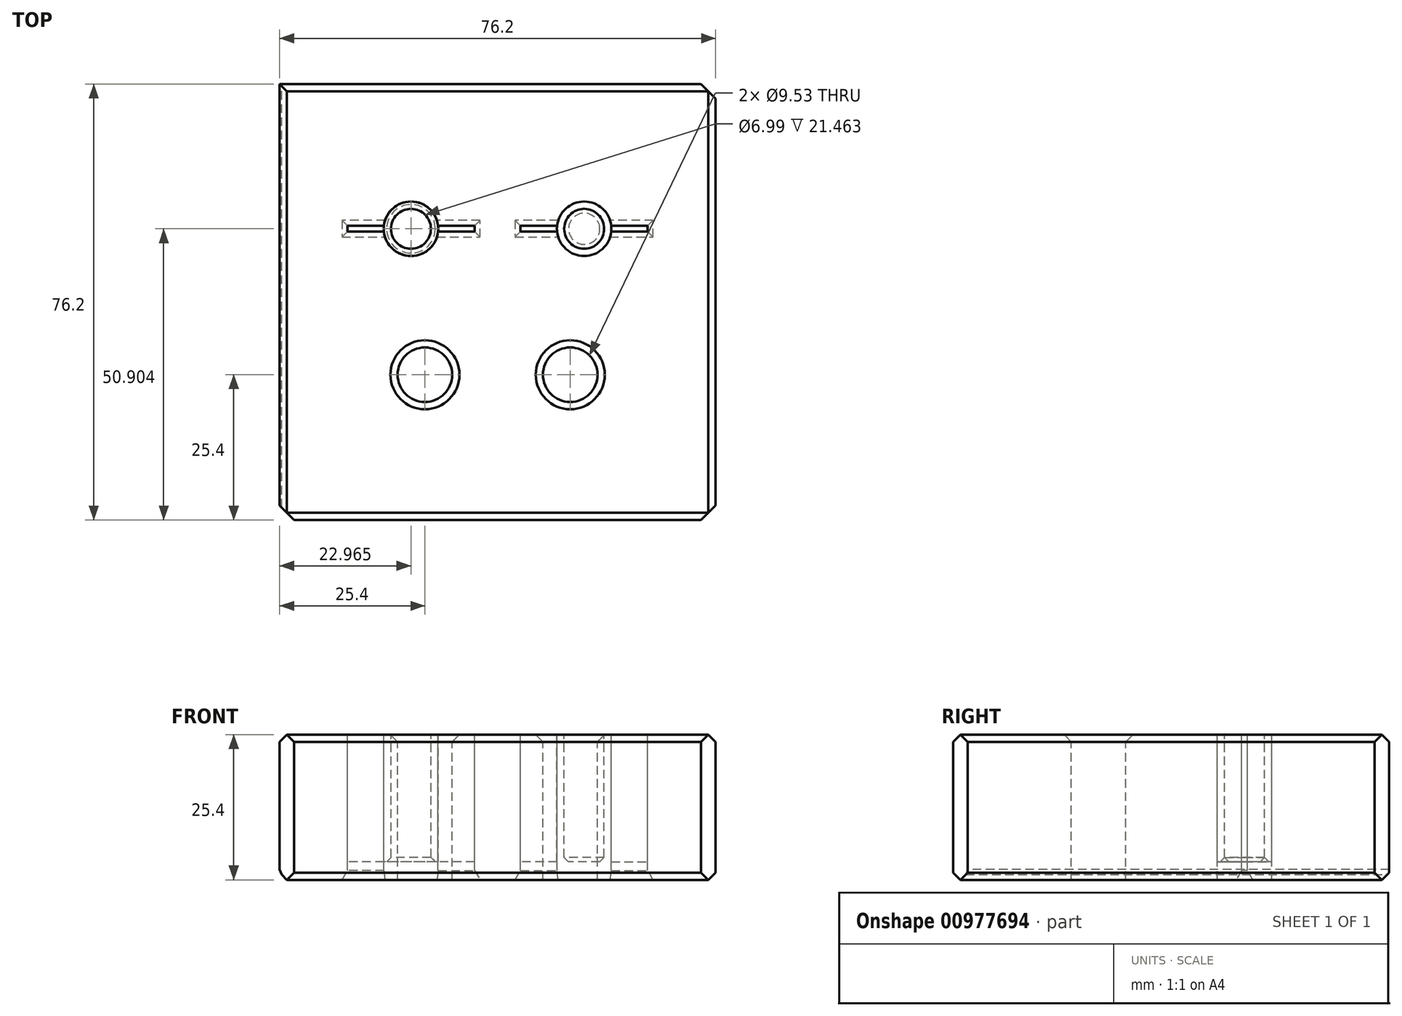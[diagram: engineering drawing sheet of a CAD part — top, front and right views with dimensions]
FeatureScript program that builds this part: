
annotation { "Feature Type Name" : "Feature", "Feature Type Description" : "" }
export const myFeature = defineFeature(function(context is Context, id is Id, definition is map)
    precondition{}
    {
        {
            var Q0;
            Q0=qCreatedBy(makeId("Top.planeOp"),FACE);
            var sketch = newSketch(context, id + "F0", { "sketchPlane" : qUnion([Q0])});
            skLineSegment(sketch, "E0.bottom", {"start": v(-38.1, 38.1) * mm, "end": v(38.1, 38.1) * mm});
            skLineSegment(sketch, "E0.top", {"start": v(-38.1, -38.1) * mm, "end": v(38.1, -38.1) * mm});
            skLineSegment(sketch, "E0.left", {"start": v(-38.1, 38.1) * mm, "end": v(-38.1, -38.1) * mm});
            skLineSegment(sketch, "E0.right", {"start": v(38.1, 38.1) * mm, "end": v(38.1, -38.1) * mm});
            skPoint(sketch, "E0.middle", {"position": v(0, 0) * mm});
            skPoint(sketch, "E1", {"position": v(-25.4, 38.1) * mm});
            skPoint(sketch, "E2.MirrorP", {"position": v(-25.4, -38.1) * mm});
            skPoint(sketch, "E3.MirrorP", {"position": v(25.4, 38.1) * mm});
            skPoint(sketch, "E4.MirrorP", {"position": v(25.4, -38.1) * mm});
            skPoint(sketch, "E5", {"position": v(-12.7, 38.1) * mm});
            skPoint(sketch, "E6", {"position": v(0, 38.1) * mm});
            skPoint(sketch, "E7", {"position": v(12.7, 38.1) * mm});
            skPoint(sketch, "E8", {"position": v(-12.7, -38.1) * mm});
            skPoint(sketch, "E9", {"position": v(-38.1, 25.4) * mm});
            skPoint(sketch, "E10", {"position": v(-38.1, 12.7) * mm});
            skPoint(sketch, "E11", {"position": v(-38.1, 0) * mm});
            skPoint(sketch, "E12.MirrorP", {"position": v(-38.1, -12.7) * mm});
            skPoint(sketch, "E13.MirrorP", {"position": v(-38.1, -25.4) * mm});
            skPoint(sketch, "E14.MirrorP", {"position": v(38.1, -25.4) * mm});
            skPoint(sketch, "E15.MirrorP", {"position": v(38.1, -12.7) * mm});
            skPoint(sketch, "E16.MirrorP", {"position": v(38.1, 0) * mm});
            skPoint(sketch, "E17.MirrorP", {"position": v(38.1, 12.7) * mm});
            skPoint(sketch, "E18.MirrorP", {"position": v(38.1, 25.4) * mm});
            skPoint(sketch, "E19", {"position": v(12.7, -38.1) * mm});
            skPoint(sketch, "E20", {"position": v(0, -38.1) * mm});
            skPoint(sketch, "E21", {"position": v(0, -25.4) * mm});
            skPoint(sketch, "E22", {"position": v(12.7, -25.4) * mm});
            skPoint(sketch, "E23", {"position": v(12.7, 25.4) * mm});
            skPoint(sketch, "E24", {"position": v(12.7, 0) * mm});
            skPoint(sketch, "E25", {"position": v(-13.1, 0) * mm});
            skLineSegment(sketch, "E26", {"start": v(0, 38.1) * mm, "end": v(0, -38.1) * mm});
            skPoint(sketch, "E27", {"position": v(-15.13, 12.8) * mm});
            skPoint(sketch, "E28", {"position": v(0, 12.7) * mm});
            skPoint(sketch, "E29", {"position": v(12.7, 12.7) * mm});
            skPoint(sketch, "E30", {"position": v(0, -12.7) * mm});
            skPoint(sketch, "E31", {"position": v(-12.7, -12.7) * mm});
            skPoint(sketch, "E32", {"position": v(12.7, -12.7) * mm});
            skPoint(sketch, "E33", {"position": v(53.16, 13.21) * mm});
            skCircle(sketch, "E34", {"center": v(-15.13, 12.8) * mm, "radius": 4.76 * mm});
            skCircle(sketch, "E35.MirrorC", {"center": v(15.13, 12.8) * mm, "radius": 4.76 * mm});
            skCircle(sketch, "E36.MirrorC", {"center": v(12.7, -12.7) * mm, "radius": 4.76 * mm});
            skCircle(sketch, "E37.MirrorC", {"center": v(-12.7, -12.7) * mm, "radius": 4.76 * mm});
            skLineSegment(sketch, "E38.left", {"start": v(-26.25, 13.31) * mm, "end": v(-26.25, 12.3) * mm});
            skLineSegment(sketch, "E38.right", {"start": v(-4.02, 13.31) * mm, "end": v(-4.02, 12.3) * mm});
            skArc(sketch, "E39", {"start": v(-10.4, 12.3) * mm, "mid": v(-10.37, 12.8) * mm, "end": v(-10.4, 13.31) * mm});
            skArc(sketch, "E40", {"start": v(-19.87, 13.31) * mm, "mid": v(-19.9, 12.8) * mm, "end": v(-19.87, 12.3) * mm});
            skLineSegment(sketch, "E41", {"start": v(-19.87, 13.31) * mm, "end": v(-26.25, 13.31) * mm});
            skLineSegment(sketch, "E42", {"start": v(-26.25, 12.3) * mm, "end": v(-19.87, 12.3) * mm});
            skLineSegment(sketch, "E43", {"start": v(-10.4, 13.31) * mm, "end": v(-4.02, 13.31) * mm});
            skLineSegment(sketch, "E44", {"start": v(-4.02, 12.3) * mm, "end": v(-10.4, 12.3) * mm});
            skCircle(sketch, "E45", {"center": v(-15.13, 12.8) * mm, "radius": 3.5 * mm});
            skCircle(sketch, "E46.MirrorC", {"center": v(15.13, 12.8) * mm, "radius": 3.5 * mm});
            skLineSegment(sketch, "E47.MirrorCS", {"start": v(10.4, 13.31) * mm, "end": v(4.02, 13.31) * mm});
            skLineSegment(sketch, "E48.MirrorCS", {"start": v(4.02, 12.3) * mm, "end": v(10.4, 12.3) * mm});
            skLineSegment(sketch, "E49.MirrorCS", {"start": v(4.02, 13.31) * mm, "end": v(4.02, 12.3) * mm});
            skLineSegment(sketch, "E50.MirrorCS", {"start": v(19.87, 13.31) * mm, "end": v(26.25, 13.31) * mm});
            skLineSegment(sketch, "E51.MirrorCS", {"start": v(26.25, 13.31) * mm, "end": v(26.25, 12.3) * mm});
            skLineSegment(sketch, "E52.MirrorCS", {"start": v(26.25, 12.3) * mm, "end": v(19.87, 12.3) * mm});
            skSolve(sketch);
        }
        {
            var Q0;
            {var subQ5=sQuery(id+"F0.wireOp",EDGE,"E0.left");Q0=makeQuery(id+"F0.imprint","IMPRINT",FACE,{"disambiguationData":[TD([[makeQuery(id+"F0.imprint","IMPRINT",EDGE,{"derivedFrom":subQ5}),1.0]])]});}
            var Q1;
            {var subQ1=sQuery(id+"F0.wireOp",EDGE,"E0.right");Q1=makeQuery(id+"F0.imprint","IMPRINT",FACE,{"disambiguationData":[TD([[makeQuery(id+"F0.imprint","IMPRINT",EDGE,{"derivedFrom":subQ1}),-1.0]])]});}
            extrude(context, id + "F1", {"entities" : qUnion([Q0, Q1]), "oppositeDirection" : true, "depth" : 25.4 * mm, "offsetDistance" : 25.4 * mm});
        }
        {
            var Q0;
            Q0=makeQuery(id+"F1.opExtrude","SWEPT_EDGE",EDGE,{"disambiguationData":[OSD([sQuery(id+"F0.wireOp",EDGE,"E0.top"),sQuery(id+"F0.wireOp",EDGE,"E0.right")])]});
            var Q1;
            Q1=makeQuery(id+"F1.opExtrude","SWEPT_EDGE",EDGE,{"disambiguationData":[OSD([sQuery(id+"F0.wireOp",EDGE,"E0.bottom"),sQuery(id+"F0.wireOp",EDGE,"E0.right")])]});
            var Q2;
            Q2=makeQuery(id+"F1.opExtrude","SWEPT_EDGE",EDGE,{"disambiguationData":[OSD([sQuery(id+"F0.wireOp",EDGE,"E0.top"),sQuery(id+"F0.wireOp",EDGE,"E0.left")])]});
            chamfer(context, id + "F2", {"entities" : qUnion([Q0, Q1, Q2]), "width" : 2.54 * mm, "tangentPropagation" : true});
        }
        {
            var Q0;
            Q0=makeQuery(id+"F1.opExtrude","CAP_EDGE",EDGE,{"disambiguationData":[OSD([sQuery(id+"F0.wireOp",EDGE,"E0.top")])],"isStart":true});
            var Q1;
            Q1=makeQuery(id+"F1.opExtrude","CAP_EDGE",EDGE,{"disambiguationData":[OSD([sQuery(id+"F0.wireOp",EDGE,"E0.bottom")])],"isStart":true});
            var Q2;
            Q2=makeQuery(id+"F1.opExtrude","CAP_EDGE",EDGE,{"disambiguationData":[OSD([sQuery(id+"F0.wireOp",EDGE,"E0.right")])],"isStart":true});
            var Q3;
            Q3=makeQuery(id+"F1.opExtrude","CAP_EDGE",EDGE,{"disambiguationData":[OSD([sQuery(id+"F0.wireOp",EDGE,"E0.right")])],"isStart":false});
            var Q4;
            Q4=makeQuery(id+"F1.opExtrude","CAP_EDGE",EDGE,{"disambiguationData":[OSD([sQuery(id+"F0.wireOp",EDGE,"E0.top")])],"isStart":false});
            var Q5;
            Q5=makeQuery(id+"F1.opExtrude","CAP_EDGE",EDGE,{"disambiguationData":[OSD([sQuery(id+"F0.wireOp",EDGE,"E0.bottom")])],"isStart":false});
            var Q6;
            Q6=makeQuery(id+"F1.opExtrude","CAP_EDGE",EDGE,{"disambiguationData":[OSD([sQuery(id+"F0.wireOp",EDGE,"E0.left")])],"isStart":false});
            chamfer(context, id + "F3", {"entities" : qUnion([Q0, Q1, Q2, Q3, Q4, Q5, Q6]), "width" : 1.27 * mm, "tangentPropagation" : true});
        }
        {
            var Q0;
            Q0=makeQuery(id+"F1.opExtrude","CAP_EDGE",EDGE,{"disambiguationData":[OSD([sQuery(id+"F0.wireOp",EDGE,"E0.left")])],"isStart":true});
            var Q1;
            {var subQ0=sQuery(id+"F0.wireOp",EDGE,"E0.left");Q1=makeQuery(id+"F3.opChamfer","BLEND_EDGE",EDGE,{"blendedFrom":[makeQuery(id+"F1.opExtrude","CAP_EDGE",EDGE,{"disambiguationData":[OSD([subQ0])],"isStart":false}),makeQuery(id+"F1.opExtrude","SWEPT_FACE",FACE,{"disambiguationData":[OSD([subQ0])]})],"blendedInto":[makeQuery(id+"F1.opExtrude","SWEPT_FACE",FACE,{"disambiguationData":[OSD([subQ0])]})]});}
            var Q2;
            Q2=makeQuery(id+"F1.opExtrude","CAP_EDGE",EDGE,{"disambiguationData":[OSD([sQuery(id+"F0.wireOp",EDGE,"E37.MirrorC")])],"isStart":true});
            var Q3;
            Q3=makeQuery(id+"F1.opExtrude","CAP_EDGE",EDGE,{"disambiguationData":[OSD([sQuery(id+"F0.wireOp",EDGE,"E36.MirrorC")])],"isStart":true});
            chamfer(context, id + "F4", {"entities" : qUnion([Q0, Q1, Q2, Q3]), "width" : 1.27 * mm, "tangentPropagation" : true});
        }
        {
            var Q0;
            Q0=makeQuery(id+"F0.imprint","IMPRINT",FACE,{"disambiguationData":[TD([[makeQuery(id+"F0.imprint","IMPRINT",EDGE,{"derivedFrom":sQuery(id+"F0.wireOp",EDGE,"E46.MirrorC")}),1.0]])]});
            var Q1;
            Q1=makeQuery(id+"F0.imprint","IMPRINT",FACE,{"disambiguationData":[TD([[makeQuery(id+"F0.imprint","IMPRINT",EDGE,{"derivedFrom":sQuery(id+"F0.wireOp",EDGE,"E45")}),-1.0]])]});
            var Q2;
            Q2=sQuery(id+"F0.wireOp",EDGE,"E46.MirrorC");
            var Q3;
            Q3=sQuery(id+"F0.wireOp",EDGE,"E35.MirrorC");
            extrude(context, id + "F5", {"entities" : qUnion([Q0, Q1]), "surfaceEntities" : qUnion([Q2, Q3]), "oppositeDirection" : true, "depth" : 22.22 * mm, "offsetDistance" : 25.4 * mm});
        }
        {
            var Q0;
            Q0=makeQuery(id+"F0.imprint","IMPRINT",FACE,{"disambiguationData":[TD([[makeQuery(id+"F0.imprint","IMPRINT",EDGE,{"derivedFrom":sQuery(id+"F0.wireOp",EDGE,"E38.right")}),-1.0]])]});
            var Q1;
            Q1=makeQuery(id+"F0.imprint","IMPRINT",FACE,{"disambiguationData":[TD([[makeQuery(id+"F0.imprint","IMPRINT",EDGE,{"derivedFrom":sQuery(id+"F0.wireOp",EDGE,"E38.left")}),1.0]])]});
            extrude(context, id + "F6", {"entities" : qUnion([Q0, Q1]), "oppositeDirection" : true, "depth" : 22.22 * mm, "offsetDistance" : 25.4 * mm});
        }
        {
            var Q0;
            {var subQ0=sQuery(id+"F0.wireOp",EDGE,"E47.MirrorCS");Q0=makeQuery(id+"F0.imprint","IMPRINT",FACE,{"disambiguationData":[TD([[makeQuery(id+"F0.imprint","IMPRINT",EDGE,{"derivedFrom":subQ0}),1.0]])]});}
            var Q1;
            {var subQ0=sQuery(id+"F0.wireOp",EDGE,"E50.MirrorCS");Q1=makeQuery(id+"F0.imprint","IMPRINT",FACE,{"disambiguationData":[TD([[makeQuery(id+"F0.imprint","IMPRINT",EDGE,{"derivedFrom":subQ0}),-1.0]])]});}
            extrude(context, id + "F7", {"entities" : qUnion([Q0, Q1]), "oppositeDirection" : true, "depth" : 22.22 * mm, "offsetDistance" : 25.4 * mm});
        }
        {
            var Q0;
            Q0=makeQuery(id+"F5.opExtrude","CAP_EDGE",EDGE,{"disambiguationData":[OSD([sQuery(id+"F0.wireOp",EDGE,"E46.MirrorC")])],"isStart":false});
            var Q1;
            Q1=makeQuery(id+"F5.opExtrude","CAP_EDGE",EDGE,{"disambiguationData":[OSD([sQuery(id+"F0.wireOp",EDGE,"E45")])],"isStart":false});
            chamfer(context, id + "F8", {"entities" : qUnion([Q0, Q1]), "width" : 0.76 * mm, "tangentPropagation" : true});
        }
        {
            var Q0;
            Q0=makeQuery(id+"F1.opExtrude","CAP_EDGE",EDGE,{"disambiguationData":[OSD([sQuery(id+"F0.wireOp",EDGE,"E42")])],"isStart":false});
            var Q1;
            Q1=makeQuery(id+"F1.opExtrude","CAP_EDGE",EDGE,{"disambiguationData":[OSD([sQuery(id+"F0.wireOp",EDGE,"E38.left")])],"isStart":false});
            var Q2;
            Q2=makeQuery(id+"F1.opExtrude","CAP_EDGE",EDGE,{"disambiguationData":[OSD([sQuery(id+"F0.wireOp",EDGE,"E41")])],"isStart":false});
            var Q3;
            Q3=makeQuery(id+"F1.opExtrude","CAP_EDGE",EDGE,{"disambiguationData":[OSD([sQuery(id+"F0.wireOp",EDGE,"E44")])],"isStart":false});
            var Q4;
            Q4=makeQuery(id+"F1.opExtrude","CAP_EDGE",EDGE,{"disambiguationData":[OSD([sQuery(id+"F0.wireOp",EDGE,"E38.right")])],"isStart":false});
            var Q5;
            Q5=makeQuery(id+"F1.opExtrude","CAP_EDGE",EDGE,{"disambiguationData":[OSD([sQuery(id+"F0.wireOp",EDGE,"E43")])],"isStart":false});
            var Q6;
            Q6=makeQuery(id+"F1.opExtrude","CAP_EDGE",EDGE,{"disambiguationData":[OSD([sQuery(id+"F0.wireOp",EDGE,"E48.MirrorCS")])],"isStart":false});
            var Q7;
            Q7=makeQuery(id+"F1.opExtrude","CAP_EDGE",EDGE,{"disambiguationData":[OSD([sQuery(id+"F0.wireOp",EDGE,"E49.MirrorCS")])],"isStart":false});
            var Q8;
            Q8=makeQuery(id+"F1.opExtrude","CAP_EDGE",EDGE,{"disambiguationData":[OSD([sQuery(id+"F0.wireOp",EDGE,"E47.MirrorCS")])],"isStart":false});
            var Q9;
            Q9=makeQuery(id+"F1.opExtrude","CAP_EDGE",EDGE,{"disambiguationData":[OSD([sQuery(id+"F0.wireOp",EDGE,"E52.MirrorCS")])],"isStart":false});
            var Q10;
            Q10=makeQuery(id+"F1.opExtrude","CAP_EDGE",EDGE,{"disambiguationData":[OSD([sQuery(id+"F0.wireOp",EDGE,"E50.MirrorCS")])],"isStart":false});
            var Q11;
            Q11=makeQuery(id+"F1.opExtrude","CAP_EDGE",EDGE,{"disambiguationData":[OSD([sQuery(id+"F0.wireOp",EDGE,"E51.MirrorCS")])],"isStart":false});
            chamfer(context, id + "F9", {"entities" : qUnion([Q0, Q1, Q2, Q3, Q4, Q5, Q6, Q7, Q8, Q9, Q10, Q11]), "chamferType" : ChamferType.OFFSET_ANGLE, "width" : 0.95 * mm, "oppositeDirection" : false, "angle" : 60 * degree, "tangentPropagation" : true});
        }
    });
